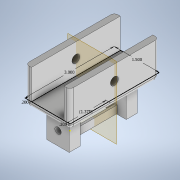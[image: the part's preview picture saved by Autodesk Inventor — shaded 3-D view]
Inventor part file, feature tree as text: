
AUTODESK INVENTOR PART (.ipt)
format: ipt  version: 2020 (Build 240168000, 168)  size: 670,720 bytes
history: native  units: in
note: dims shown in document units (in); Inventor stores cm internally (conversion verified against a paired STEP export)
features: sketch x8, extrude x5, hole x4, fillet x1, plane x1, mirror x1
ambient origin geometry x8: Origin, YZ Plane, XZ Plane, XY Plane, X Axis, Y Axis, Z Axis, Center Point
bodies: Solid1 (feature_tree)
feature tree (20):
  sketch  "Sketch1"  dims[d0=1.5in d1=3.0in]
  extrude  "Extrusion1"  Depth=3.0in
  extrude  "Extrusion2"  Depth=0.2in
  hole  "Hole1"  [1 undecoded]
  extrude  "Extrusion3"  Depth=1.0in
  hole  "Hole2"  [1 undecoded]
  fillet  "Fillet1"  Radius=0.125in
  extrude  "Extrusion4"  Depth=1.0in TaperAngle=0.0deg
  extrude  "Extrusion5"  Depth=0.125in
  hole  "Hole3"  [1 undecoded]
  hole  "Hole4"  [1 undecoded]
  sketch  "Sketch9"  dims[d23=0.45in d24=0.0787in d25=0.75in d26=0.438in d27=0.25in d28=0.5635in d29=1.0in d30=0.8108in d31=0.125in d32=0.125in d33=0.125in d34=0.5in d35=0.5in d36=90.0deg d37=0.1in d38=0.1in d39=0.125in d40=0.075in d41=0.25in d42=1.6in d43=0.0in d44=0.05in d45=0.0in d46=0.5in d47=0.5in d48=0.5in d49=0.375in d50=0.375in d51=0.375in d52=0.213in d53=0.75in d54=0.119in d55=0.25in d56=0.5635in d57=0.25in d58=0.0in d59=0.176in d60=0.75in d61=0.119in d62=0.25in d63=0.5635in d64=0.08in d65=0.0in d66=1.375in]
  plane  "Work Plane1"
  mirror  "Mirror1"
  sketch  "Sketch2"  dims[d2=0.2in d3=0.2in]
  sketch  "Sketch3"  dims[d4=1.0in d5=0.0in d6=0.2in d7=0.0in]
  sketch  "Sketch5"  dims[d8=0.5in]
  sketch  "Sketch6"  dims[d9=0.266in d10=0.75in d11=0.438in d12=0.25in d13=0.5635in d14=1.0in d15=0.8108in d16=0.5in]
  sketch  "Sketch7"  dims[d17=1.0in d18=0.75in d19=0.125in]
  sketch  "Sketch8"  dims[d20=0.125in d21=1.0in d22=0.0in]
note: 4 required parameter values undecoded (feature->parameter linkage not recoverable at this tier; creation-order binding heuristic only, values carry confidence <= 0.55)
